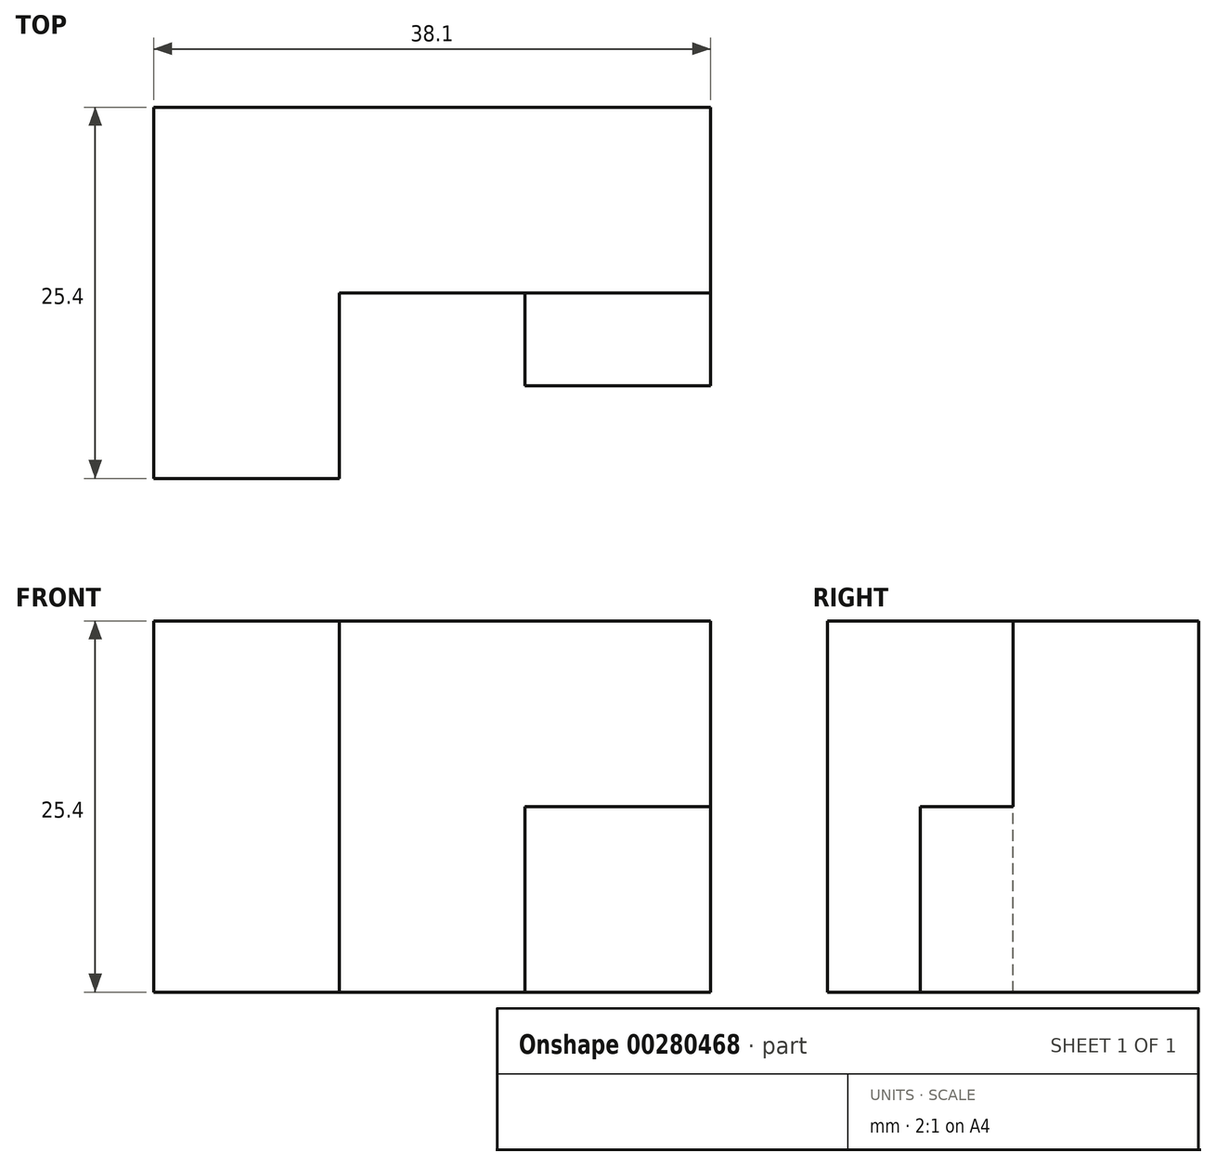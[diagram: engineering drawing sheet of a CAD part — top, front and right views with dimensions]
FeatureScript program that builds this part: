
annotation { "Feature Type Name" : "Feature", "Feature Type Description" : "" }
export const myFeature = defineFeature(function(context is Context, id is Id, definition is map)
    precondition{}
    {
        {
            var Q0;
            Q0=qCreatedBy(makeId("Top.planeOp"),FACE);
            var sketch = newSketch(context, id + "F0", { "sketchPlane" : qUnion([Q0])});
            skLineSegment(sketch, "E0", {"start": v(0, 0) * mm, "end": v(0, 25.4) * mm});
            skLineSegment(sketch, "E1", {"start": v(0, 25.4) * mm, "end": v(38.1, 25.4) * mm});
            skLineSegment(sketch, "E2", {"start": v(38.1, 25.4) * mm, "end": v(38.1, 12.7) * mm});
            skLineSegment(sketch, "E3", {"start": v(38.1, 12.7) * mm, "end": v(12.7, 12.7) * mm});
            skLineSegment(sketch, "E4", {"start": v(12.7, 12.7) * mm, "end": v(12.7, 0) * mm});
            skLineSegment(sketch, "E5", {"start": v(12.7, 0) * mm, "end": v(0, 0) * mm});
            skSolve(sketch);
        }
        {
            var Q0;
            Q0=makeQuery(id+"F0.imprint","IMPRINT",FACE,{"disambiguationData":[TD([[makeQuery(id+"F0.imprint","IMPRINT",EDGE,{"derivedFrom":sQuery(id+"F0.wireOp",EDGE,"E0")}),-1.0]])]});
            extrude(context, id + "F1", {"entities" : qUnion([Q0]), "depth" : 25.4 * mm});
        }
        {
            var Q0;
            Q0=makeQuery(id+"F1.opExtrude","SWEPT_FACE",FACE,{"disambiguationData":[OSD([sQuery(id+"F0.wireOp",EDGE,"E3")])]});
            var sketch = newSketch(context, id + "F2", { "sketchPlane" : qUnion([Q0])});
            skPoint(sketch, "E6.oppositeSnap0", {"position": v(12.7, 12.7) * mm});
            skLineSegment(sketch, "E6.bottom", {"start": v(38.1, 0) * mm, "end": v(25.4, 0) * mm});
            skLineSegment(sketch, "E6.top", {"start": v(38.1, 12.7) * mm, "end": v(25.4, 12.7) * mm});
            skLineSegment(sketch, "E6.left", {"start": v(38.1, 0) * mm, "end": v(38.1, 12.7) * mm});
            skLineSegment(sketch, "E6.right", {"start": v(25.4, 0) * mm, "end": v(25.4, 12.7) * mm});
            skSolve(sketch);
        }
        {
            var Q0;
            Q0=makeQuery(id+"F2.imprint","IMPRINT",FACE,{"disambiguationData":[TD([[makeQuery(id+"F2.imprint","IMPRINT",EDGE,{"derivedFrom":sQuery(id+"F2.wireOp",EDGE,"E6.bottom")}),-1.0]])]});
            extrude(context, id + "F3", {"entities" : qUnion([Q0]), "operationType" : NewBodyOperationType.ADD, "depth" : 6.35 * mm});
        }
    });
